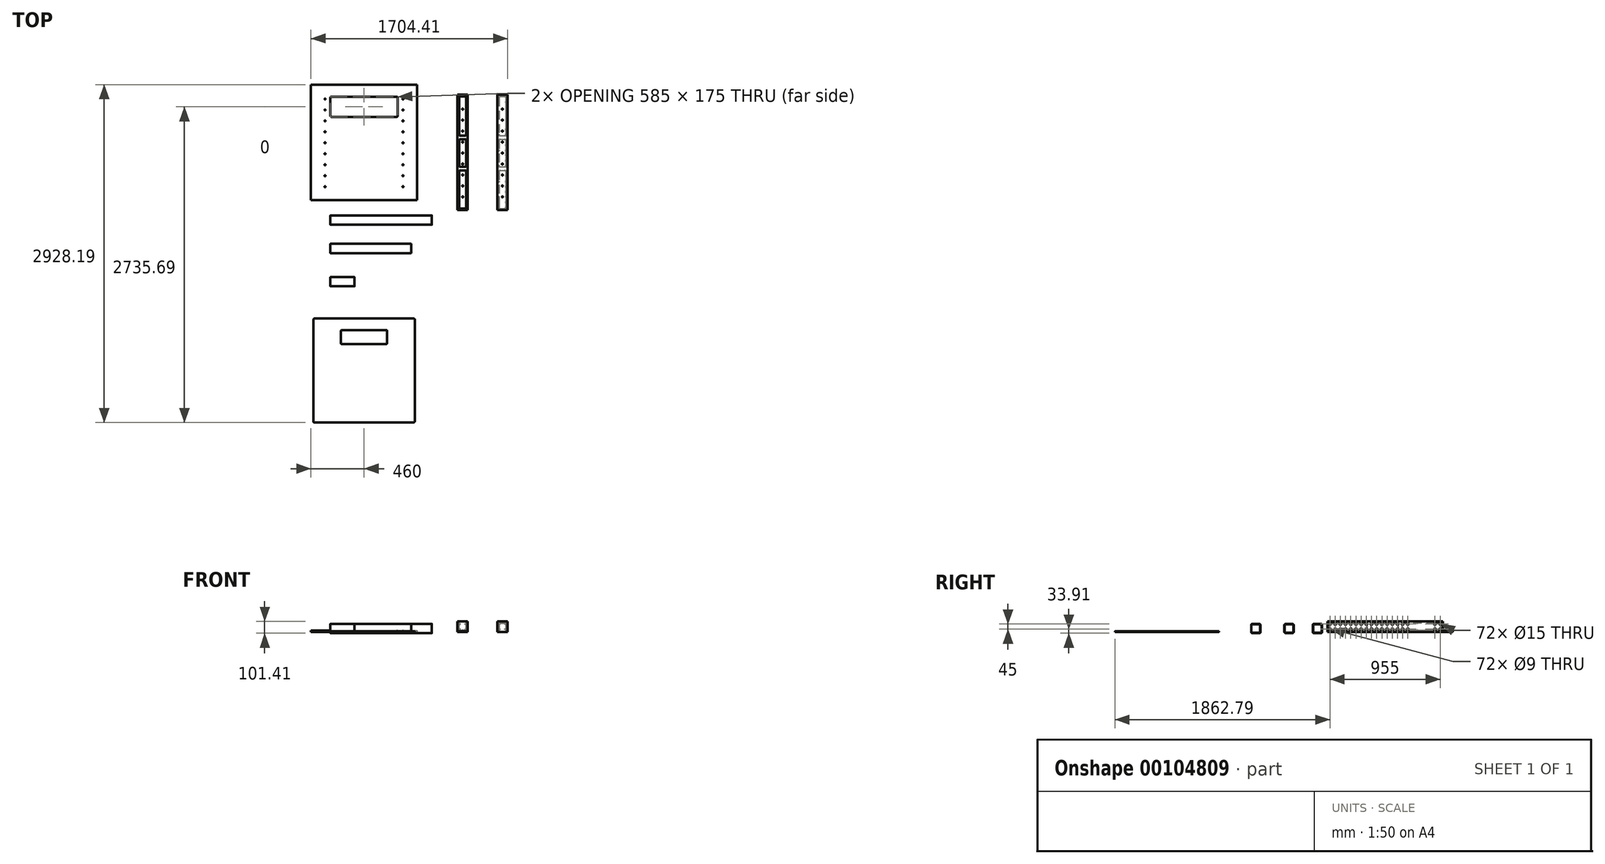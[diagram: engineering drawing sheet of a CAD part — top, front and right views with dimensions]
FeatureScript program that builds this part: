
annotation { "Feature Type Name" : "Feature", "Feature Type Description" : "" }
export const myFeature = defineFeature(function(context is Context, id is Id, definition is map)
    precondition{}
    {
        {
            var Q0;
            Q0=qCreatedBy(makeId("Top.planeOp"),FACE);
            var sketch = newSketch(context, id + "F0", { "sketchPlane" : qUnion([Q0])});
            skLineSegment(sketch, "E0.bottom", {"start": v(-167.5, 789.91) * mm, "end": v(752.5, 789.91) * mm});
            skLineSegment(sketch, "E0.top", {"start": v(-167.5, -210.09) * mm, "end": v(752.5, -210.09) * mm});
            skLineSegment(sketch, "E0.left", {"start": v(-167.5, 789.91) * mm, "end": v(-167.5, -210.09) * mm});
            skLineSegment(sketch, "E0.right", {"start": v(752.5, 789.91) * mm, "end": v(752.5, -210.09) * mm});
            skLineSegment(sketch, "E1.bottom", {"start": v(10, 684.91) * mm, "end": v(575, 684.91) * mm});
            skLineSegment(sketch, "E1.top", {"start": v(10, 509.91) * mm, "end": v(575, 509.91) * mm});
            skLineSegment(sketch, "E1.left", {"start": v(0, 674.91) * mm, "end": v(0, 519.91) * mm});
            skLineSegment(sketch, "E1.right", {"start": v(585, 674.91) * mm, "end": v(585, 519.91) * mm});
            skPoint(sketch, "E2.visualSharp", {"position": v(0, 684.91) * mm});
            skArc(sketch, "E2.filletArc", {"start": v(10, 684.91) * mm, "mid": v(2.93, 681.98) * mm, "end": v(0, 674.91) * mm});
            skPoint(sketch, "E3.visualSharp", {"position": v(0, 509.91) * mm});
            skArc(sketch, "E3.filletArc", {"start": v(0, 519.91) * mm, "mid": v(2.93, 512.84) * mm, "end": v(10, 509.91) * mm});
            skPoint(sketch, "E4.visualSharp", {"position": v(585, 684.91) * mm});
            skArc(sketch, "E4.filletArc", {"start": v(585, 674.91) * mm, "mid": v(582.07, 681.98) * mm, "end": v(575, 684.91) * mm});
            skPoint(sketch, "E5.visualSharp", {"position": v(585, 509.91) * mm});
            skArc(sketch, "E5.filletArc", {"start": v(575, 509.91) * mm, "mid": v(582.07, 512.84) * mm, "end": v(585, 519.91) * mm});
            skLineSegment(sketch, "E6.bottom", {"start": v(1101.91, 702) * mm, "end": v(1191.91, 702) * mm});
            skLineSegment(sketch, "E6.top", {"start": v(1101.91, -298) * mm, "end": v(1191.91, -298) * mm});
            skLineSegment(sketch, "E6.left", {"start": v(1101.91, 702) * mm, "end": v(1101.91, -298) * mm});
            skLineSegment(sketch, "E6.right", {"start": v(1191.91, 702) * mm, "end": v(1191.91, -298) * mm});
            skPoint(sketch, "E7", {"position": v(292.5, 684.91) * mm});
            skPoint(sketch, "E8", {"position": v(292.5, 789.91) * mm});
            skLineSegment(sketch, "E9.bottom", {"start": v(-137.5, -1238.28) * mm, "end": v(722.5, -1238.28) * mm});
            skLineSegment(sketch, "E9.top", {"start": v(-137.5, -2138.28) * mm, "end": v(722.5, -2138.28) * mm});
            skLineSegment(sketch, "E9.left", {"start": v(-147.5, -1248.28) * mm, "end": v(-147.5, -2128.28) * mm});
            skLineSegment(sketch, "E9.right", {"start": v(732.5, -1248.28) * mm, "end": v(732.5, -2128.28) * mm});
            skLineSegment(sketch, "E10.bottom", {"start": v(97.5, -1338.28) * mm, "end": v(487.5, -1338.28) * mm});
            skLineSegment(sketch, "E10.top", {"start": v(97.5, -1458.28) * mm, "end": v(487.5, -1458.28) * mm});
            skLineSegment(sketch, "E10.left", {"start": v(92.5, -1343.28) * mm, "end": v(92.5, -1453.28) * mm});
            skLineSegment(sketch, "E10.right", {"start": v(492.5, -1343.28) * mm, "end": v(492.5, -1453.28) * mm});
            skPoint(sketch, "E11.visualSharp", {"position": v(92.5, -1338.28) * mm});
            skArc(sketch, "E11.filletArc", {"start": v(97.5, -1338.28) * mm, "mid": v(93.97, -1339.74) * mm, "end": v(92.5, -1343.28) * mm});
            skPoint(sketch, "E12.visualSharp", {"position": v(92.5, -1458.28) * mm});
            skArc(sketch, "E12.filletArc", {"start": v(92.5, -1453.28) * mm, "mid": v(93.97, -1456.81) * mm, "end": v(97.5, -1458.28) * mm});
            skPoint(sketch, "E13.visualSharp", {"position": v(492.5, -1458.28) * mm});
            skArc(sketch, "E13.filletArc", {"start": v(487.5, -1458.28) * mm, "mid": v(491.04, -1456.81) * mm, "end": v(492.5, -1453.28) * mm});
            skPoint(sketch, "E14.visualSharp", {"position": v(492.5, -1338.28) * mm});
            skArc(sketch, "E14.filletArc", {"start": v(492.5, -1343.28) * mm, "mid": v(491.04, -1339.74) * mm, "end": v(487.5, -1338.28) * mm});
            skPoint(sketch, "E15.visualSharp", {"position": v(-147.5, -2138.28) * mm});
            skArc(sketch, "E15.filletArc", {"start": v(-147.5, -2128.28) * mm, "mid": v(-144.56, -2135.35) * mm, "end": v(-137.5, -2138.28) * mm});
            skPoint(sketch, "E16.visualSharp", {"position": v(732.5, -2138.28) * mm});
            skArc(sketch, "E16.filletArc", {"start": v(722.5, -2138.28) * mm, "mid": v(729.58, -2135.35) * mm, "end": v(732.5, -2128.28) * mm});
            skPoint(sketch, "E17.visualSharp", {"position": v(732.5, -1238.28) * mm});
            skArc(sketch, "E17.filletArc", {"start": v(732.5, -1248.28) * mm, "mid": v(729.58, -1241.2) * mm, "end": v(722.5, -1238.28) * mm});
            skPoint(sketch, "E18.visualSharp", {"position": v(-147.5, -1238.28) * mm});
            skArc(sketch, "E18.filletArc", {"start": v(-137.5, -1238.28) * mm, "mid": v(-144.56, -1241.2) * mm, "end": v(-147.5, -1248.28) * mm});
            skSolve(sketch);
        }
        {
            var Q0;
            Q0=makeQuery(id+"F0.imprint","IMPRINT",FACE,{"disambiguationData":[TD([[makeQuery(id+"F0.imprint","IMPRINT",EDGE,{"derivedFrom":sQuery(id+"F0.wireOp",EDGE,"E0.bottom")}),-1.0]])]});
            extrude(context, id + "F1", {"entities" : qUnion([Q0]), "depth" : 10 * mm});
        }
        {
            var Q0;
            Q0=makeQuery(id+"F0.imprint","IMPRINT",FACE,{"disambiguationData":[TD([[makeQuery(id+"F0.imprint","IMPRINT",EDGE,{"derivedFrom":sQuery(id+"F0.wireOp",EDGE,"E6.bottom")}),-1.0]])]});
            extrude(context, id + "F2", {"entities" : qUnion([Q0]), "depth" : 90 * mm});
        }
        {
            var Q0;
            Q0=makeQuery(id+"F2.opExtrude","SWEPT_FACE",FACE,{"disambiguationData":[OSD([sQuery(id+"F0.wireOp",EDGE,"E6.right")])]});
            var sketch = newSketch(context, id + "F3", { "sketchPlane" : qUnion([Q0])});
            skLineSegment(sketch, "E19", {"start": v(-298, 67.5) * mm, "end": v(702, 67.5) * mm});
            skLineSegment(sketch, "E20", {"start": v(-298, 22.5) * mm, "end": v(702, 22.5) * mm});
            skLineSegment(sketch, "E21", {"start": v(-275.5, 90) * mm, "end": v(-275.5, 0) * mm});
            skLineSegment(sketch, "E22", {"start": v(-230.5, 90) * mm, "end": v(-230.5, 0) * mm});
            skLineSegment(sketch, "E23", {"start": v(-185.5, 90) * mm, "end": v(-185.5, 0) * mm});
            skLineSegment(sketch, "E24", {"start": v(-140.5, 90) * mm, "end": v(-140.5, 0) * mm});
            skPoint(sketch, "E25", {"position": v(-275.5, 67.5) * mm});
            skPoint(sketch, "E26", {"position": v(-230.5, 67.5) * mm});
            skPoint(sketch, "E27", {"position": v(-140.5, 67.5) * mm});
            skPoint(sketch, "E28", {"position": v(-185.5, 67.5) * mm});
            skPoint(sketch, "E29", {"position": v(-185.5, 22.5) * mm});
            skPoint(sketch, "E30", {"position": v(-140.5, 22.5) * mm});
            skPoint(sketch, "E31", {"position": v(-230.5, 22.5) * mm});
            skPoint(sketch, "E32", {"position": v(-275.5, 22.5) * mm});
            skLineSegment(sketch, "E33", {"start": v(-95.5, 90) * mm, "end": v(-95.5, 0) * mm});
            skLineSegment(sketch, "E34", {"start": v(-50.5, 90) * mm, "end": v(-50.5, 0) * mm});
            skLineSegment(sketch, "E35", {"start": v(-5.5, 90) * mm, "end": v(-5.5, 0) * mm});
            skLineSegment(sketch, "E36", {"start": v(39.5, 90) * mm, "end": v(39.5, 0) * mm});
            skLineSegment(sketch, "E37", {"start": v(84.5, 90) * mm, "end": v(84.5, 0) * mm});
            skLineSegment(sketch, "E38", {"start": v(129.5, 90) * mm, "end": v(129.5, 0) * mm});
            skLineSegment(sketch, "E39", {"start": v(174.5, 90) * mm, "end": v(174.5, 0) * mm});
            skLineSegment(sketch, "E40", {"start": v(219.5, 90) * mm, "end": v(219.5, 0) * mm});
            skLineSegment(sketch, "E41", {"start": v(264.5, 90) * mm, "end": v(264.5, 0) * mm});
            skLineSegment(sketch, "E42", {"start": v(309.5, 90) * mm, "end": v(309.5, 0) * mm});
            skPoint(sketch, "E43", {"position": v(-95.5, 67.5) * mm});
            skPoint(sketch, "E44", {"position": v(-95.5, 22.5) * mm});
            skPoint(sketch, "E45", {"position": v(-50.5, 67.5) * mm});
            skPoint(sketch, "E46", {"position": v(-50.5, 22.5) * mm});
            skPoint(sketch, "E47", {"position": v(-5.5, 67.5) * mm});
            skPoint(sketch, "E48", {"position": v(-5.5, 22.5) * mm});
            skPoint(sketch, "E49", {"position": v(39.5, 67.5) * mm});
            skPoint(sketch, "E50", {"position": v(39.5, 22.5) * mm});
            skPoint(sketch, "E51", {"position": v(84.5, 67.5) * mm});
            skPoint(sketch, "E52", {"position": v(84.5, 22.5) * mm});
            skPoint(sketch, "E53", {"position": v(129.5, 67.5) * mm});
            skPoint(sketch, "E54", {"position": v(129.5, 22.5) * mm});
            skPoint(sketch, "E55", {"position": v(174.5, 67.5) * mm});
            skPoint(sketch, "E56", {"position": v(174.5, 22.5) * mm});
            skPoint(sketch, "E57", {"position": v(219.5, 67.5) * mm});
            skPoint(sketch, "E58", {"position": v(219.5, 22.5) * mm});
            skPoint(sketch, "E59", {"position": v(264.5, 67.5) * mm});
            skPoint(sketch, "E60", {"position": v(264.5, 22.5) * mm});
            skPoint(sketch, "E61", {"position": v(309.5, 22.5) * mm});
            skPoint(sketch, "E62", {"position": v(309.5, 67.5) * mm});
            skLineSegment(sketch, "E63", {"start": v(679.5, 90) * mm, "end": v(679.5, 0) * mm});
            skLineSegment(sketch, "E64", {"start": v(634.5, 90) * mm, "end": v(634.5, 0) * mm});
            skPoint(sketch, "E65", {"position": v(634.5, 67.5) * mm});
            skPoint(sketch, "E66", {"position": v(634.5, 22.5) * mm});
            skPoint(sketch, "E67", {"position": v(679.5, 67.5) * mm});
            skPoint(sketch, "E68", {"position": v(679.5, 22.5) * mm});
            skLineSegment(sketch, "E69", {"start": v(354.5, 0) * mm, "end": v(354.5, 90) * mm});
            skLineSegment(sketch, "E70", {"start": v(399.5, 0) * mm, "end": v(399.5, 90) * mm});
            skPoint(sketch, "E71", {"position": v(399.5, 22.5) * mm});
            skPoint(sketch, "E72", {"position": v(354.5, 22.5) * mm});
            skPoint(sketch, "E73", {"position": v(354.5, 67.5) * mm});
            skPoint(sketch, "E74", {"position": v(399.5, 67.5) * mm});
            skSolve(sketch);
        }
        {
            var Q0;
            Q0=sQuery(id+"F3.wireOp",VERTEX,"E25");
            var Q1;
            Q1=sQuery(id+"F3.wireOp",VERTEX,"E32");
            var Q2;
            Q2=sQuery(id+"F3.wireOp",VERTEX,"E26");
            var Q3;
            Q3=sQuery(id+"F3.wireOp",VERTEX,"E31");
            var Q4;
            Q4=sQuery(id+"F3.wireOp",VERTEX,"E28");
            var Q5;
            Q5=sQuery(id+"F3.wireOp",VERTEX,"E29");
            var Q6;
            Q6=sQuery(id+"F3.wireOp",VERTEX,"E30");
            var Q7;
            Q7=sQuery(id+"F3.wireOp",VERTEX,"E27");
            var Q8;
            Q8=sQuery(id+"F3.wireOp",VERTEX,"E43");
            var Q9;
            Q9=sQuery(id+"F3.wireOp",VERTEX,"E44");
            var Q10;
            Q10=sQuery(id+"F3.wireOp",VERTEX,"E46");
            var Q11;
            Q11=sQuery(id+"F3.wireOp",VERTEX,"E45");
            var Q12;
            Q12=sQuery(id+"F3.wireOp",VERTEX,"E47");
            var Q13;
            Q13=sQuery(id+"F3.wireOp",VERTEX,"E48");
            var Q14;
            Q14=sQuery(id+"F3.wireOp",VERTEX,"E50");
            var Q15;
            Q15=sQuery(id+"F3.wireOp",VERTEX,"E49");
            var Q16;
            Q16=sQuery(id+"F3.wireOp",VERTEX,"E51");
            var Q17;
            Q17=sQuery(id+"F3.wireOp",VERTEX,"E52");
            var Q18;
            Q18=sQuery(id+"F3.wireOp",VERTEX,"E54");
            var Q19;
            Q19=sQuery(id+"F3.wireOp",VERTEX,"E53");
            var Q20;
            Q20=sQuery(id+"F3.wireOp",VERTEX,"E55");
            var Q21;
            Q21=sQuery(id+"F3.wireOp",VERTEX,"E56");
            var Q22;
            Q22=sQuery(id+"F3.wireOp",VERTEX,"E58");
            var Q23;
            Q23=sQuery(id+"F3.wireOp",VERTEX,"E57");
            var Q24;
            Q24=sQuery(id+"F3.wireOp",VERTEX,"E59");
            var Q25;
            Q25=sQuery(id+"F3.wireOp",VERTEX,"E60");
            var Q26;
            Q26=sQuery(id+"F3.wireOp",VERTEX,"E61");
            var Q27;
            Q27=sQuery(id+"F3.wireOp",VERTEX,"E62");
            var Q28;
            Q28=sQuery(id+"F3.wireOp",VERTEX,"E65");
            var Q29;
            Q29=sQuery(id+"F3.wireOp",VERTEX,"E66");
            var Q30;
            Q30=sQuery(id+"F3.wireOp",VERTEX,"E68");
            var Q31;
            Q31=sQuery(id+"F3.wireOp",VERTEX,"E67");
            var Q32;
            Q32=sQuery(id+"F3.wireOp",VERTEX,"E72");
            var Q33;
            Q33=sQuery(id+"F3.wireOp",VERTEX,"E73");
            var Q34;
            Q34=sQuery(id+"F3.wireOp",VERTEX,"E71");
            var Q35;
            Q35=sQuery(id+"F3.wireOp",VERTEX,"E74");
            var Q36;
            Q36=makeQuery(id+"F2.opExtrude","SWEPT_BODY",BODY,{"disambiguationData":[OSD([sQuery(id+"F0.wireOp",EDGE,"E6.bottom"),sQuery(id+"F0.wireOp",EDGE,"E6.top"),sQuery(id+"F0.wireOp",EDGE,"E6.left"),sQuery(id+"F0.wireOp",EDGE,"E6.right")])]});
            hole(context, id + "F4", {"style" : HoleStyle.C_BORE, "endStyle" : HoleEndStyle.THROUGH, "holeDiameter" : 9 * mm, "cBoreDiameter" : 15 * mm, "cBoreDepth" : 75 * mm, "locations" : qUnion([Q0, Q1, Q2, Q3, Q4, Q5, Q6, Q7, Q8, Q9, Q10, Q11, Q12, Q13, Q14, Q15, Q16, Q17, Q18, Q19, Q20, Q21, Q22, Q23, Q24, Q25, Q26, Q27, Q28, Q29, Q30, Q31, Q32, Q33, Q34, Q35]), "scope" : qUnion([Q36]), "isTappedThrough" : true});
        }
        {
            var Q0;
            Q0=makeQuery(id+"F2.opExtrude","CAP_FACE",FACE,{"disambiguationData":[OSD([sQuery(id+"F0.wireOp",EDGE,"E6.bottom"),sQuery(id+"F0.wireOp",EDGE,"E6.top"),sQuery(id+"F0.wireOp",EDGE,"E6.left"),sQuery(id+"F0.wireOp",EDGE,"E6.right")])],"isStart":false});
            var sketch = newSketch(context, id + "F5", { "sketchPlane" : qUnion([Q0])});
            skLineSegment(sketch, "E75", {"start": v(1146.91, -298) * mm, "end": v(1146.91, 702) * mm});
            skLineSegment(sketch, "E76", {"start": v(1101.91, -203) * mm, "end": v(1191.91, -203) * mm});
            skLineSegment(sketch, "E77", {"start": v(1101.91, -88) * mm, "end": v(1191.91, -88) * mm});
            skLineSegment(sketch, "E78", {"start": v(1101.91, 7) * mm, "end": v(1191.91, 7) * mm});
            skLineSegment(sketch, "E79", {"start": v(1101.91, 102) * mm, "end": v(1191.91, 102) * mm});
            skLineSegment(sketch, "E80", {"start": v(1101.91, 292) * mm, "end": v(1191.91, 292) * mm});
            skLineSegment(sketch, "E81", {"start": v(1101.91, 197) * mm, "end": v(1191.91, 197) * mm});
            skLineSegment(sketch, "E82", {"start": v(1101.91, 387) * mm, "end": v(1191.91, 387) * mm});
            skLineSegment(sketch, "E83", {"start": v(1101.91, 482) * mm, "end": v(1191.91, 482) * mm});
            skLineSegment(sketch, "E84", {"start": v(1101.91, -183) * mm, "end": v(1191.91, -183) * mm});
            skLineSegment(sketch, "E85", {"start": v(1101.91, 577) * mm, "end": v(1191.91, 577) * mm});
            skPoint(sketch, "E86", {"position": v(1146.91, -183) * mm});
            skPoint(sketch, "E87", {"position": v(1146.91, -88) * mm});
            skPoint(sketch, "E88", {"position": v(1146.91, 7) * mm});
            skPoint(sketch, "E89", {"position": v(1146.91, 102) * mm});
            skPoint(sketch, "E90", {"position": v(1146.91, 197) * mm});
            skPoint(sketch, "E91", {"position": v(1146.91, 292) * mm});
            skPoint(sketch, "E92", {"position": v(1146.91, 387) * mm});
            skPoint(sketch, "E93", {"position": v(1146.91, 482) * mm});
            skPoint(sketch, "E94", {"position": v(1146.91, 577) * mm});
            skLineSegment(sketch, "E95.bottom", {"start": v(1126.91, -283) * mm, "end": v(1166.91, -283) * mm});
            skLineSegment(sketch, "E95.top", {"start": v(1126.91, 47) * mm, "end": v(1166.91, 47) * mm});
            skLineSegment(sketch, "E95.left", {"start": v(1116.91, -273) * mm, "end": v(1116.91, 37) * mm});
            skLineSegment(sketch, "E95.right", {"start": v(1176.91, -273) * mm, "end": v(1176.91, 37) * mm});
            skLineSegment(sketch, "E96.bottom", {"start": v(1126.91, 77) * mm, "end": v(1166.91, 77) * mm});
            skLineSegment(sketch, "E96.top", {"start": v(1126.91, 317) * mm, "end": v(1166.91, 317) * mm});
            skLineSegment(sketch, "E96.left", {"start": v(1116.91, 87) * mm, "end": v(1116.91, 307) * mm});
            skLineSegment(sketch, "E96.right", {"start": v(1176.91, 87) * mm, "end": v(1176.91, 307) * mm});
            skLineSegment(sketch, "E97.bottom", {"start": v(1126.91, 347) * mm, "end": v(1166.91, 347) * mm});
            skLineSegment(sketch, "E97.top", {"start": v(1126.91, 687) * mm, "end": v(1166.91, 687) * mm});
            skLineSegment(sketch, "E97.left", {"start": v(1116.91, 357) * mm, "end": v(1116.91, 677) * mm});
            skLineSegment(sketch, "E97.right", {"start": v(1176.91, 357) * mm, "end": v(1176.91, 677) * mm});
            skPoint(sketch, "E98.visualSharp", {"position": v(1116.91, -283) * mm});
            skArc(sketch, "E98.filletArc", {"start": v(1116.91, -273) * mm, "mid": v(1119.84, -280.06) * mm, "end": v(1126.91, -283) * mm});
            skPoint(sketch, "E99.visualSharp", {"position": v(1176.91, -283) * mm});
            skArc(sketch, "E99.filletArc", {"start": v(1166.91, -283) * mm, "mid": v(1173.98, -280.06) * mm, "end": v(1176.91, -273) * mm});
            skPoint(sketch, "E100.visualSharp", {"position": v(1176.91, 47) * mm});
            skArc(sketch, "E100.filletArc", {"start": v(1176.91, 37) * mm, "mid": v(1173.98, 44.08) * mm, "end": v(1166.91, 47) * mm});
            skPoint(sketch, "E101.visualSharp", {"position": v(1116.91, 47) * mm});
            skArc(sketch, "E101.filletArc", {"start": v(1126.91, 47) * mm, "mid": v(1119.84, 44.08) * mm, "end": v(1116.91, 37) * mm});
            skPoint(sketch, "E102.visualSharp", {"position": v(1116.91, 77) * mm});
            skArc(sketch, "E102.filletArc", {"start": v(1116.91, 87) * mm, "mid": v(1119.84, 79.94) * mm, "end": v(1126.91, 77) * mm});
            skPoint(sketch, "E103.visualSharp", {"position": v(1176.91, 77) * mm});
            skArc(sketch, "E103.filletArc", {"start": v(1166.91, 77) * mm, "mid": v(1173.98, 79.94) * mm, "end": v(1176.91, 87) * mm});
            skPoint(sketch, "E104.visualSharp", {"position": v(1116.91, 317) * mm});
            skArc(sketch, "E104.filletArc", {"start": v(1126.91, 317) * mm, "mid": v(1119.84, 314.08) * mm, "end": v(1116.91, 307) * mm});
            skPoint(sketch, "E105.visualSharp", {"position": v(1176.91, 317) * mm});
            skArc(sketch, "E105.filletArc", {"start": v(1176.91, 307) * mm, "mid": v(1173.98, 314.08) * mm, "end": v(1166.91, 317) * mm});
            skPoint(sketch, "E106.visualSharp", {"position": v(1176.91, 347) * mm});
            skArc(sketch, "E106.filletArc", {"start": v(1166.91, 347) * mm, "mid": v(1173.98, 349.94) * mm, "end": v(1176.91, 357) * mm});
            skPoint(sketch, "E107.visualSharp", {"position": v(1116.91, 347) * mm});
            skArc(sketch, "E107.filletArc", {"start": v(1116.91, 357) * mm, "mid": v(1119.84, 349.94) * mm, "end": v(1126.91, 347) * mm});
            skPoint(sketch, "E108.visualSharp", {"position": v(1116.91, 687) * mm});
            skArc(sketch, "E108.filletArc", {"start": v(1126.91, 687) * mm, "mid": v(1119.84, 684.08) * mm, "end": v(1116.91, 677) * mm});
            skPoint(sketch, "E109.visualSharp", {"position": v(1176.91, 687) * mm});
            skArc(sketch, "E109.filletArc", {"start": v(1176.91, 677) * mm, "mid": v(1173.98, 684.08) * mm, "end": v(1166.91, 687) * mm});
            skSolve(sketch);
        }
        {
            var Q0;
            Q0=makeQuery(id+"F2.opExtrude","SWEPT_BODY",BODY,{"disambiguationData":[OSD([sQuery(id+"F0.wireOp",EDGE,"E6.bottom"),sQuery(id+"F0.wireOp",EDGE,"E6.top"),sQuery(id+"F0.wireOp",EDGE,"E6.left"),sQuery(id+"F0.wireOp",EDGE,"E6.right")])]});
            transform(context, id + "F6", {"entities" : qUnion([Q0]), "transformType" : TransformType.TRANSLATION_3D, "dx" : 345 * mm, "dy" : 0 * mm, "dz" : 0 * mm, "makeCopy" : true});
        }
        {
            var Q0;
            Q0=sQuery(id+"F5.wireOp",VERTEX,"E86");
            var Q1;
            Q1=sQuery(id+"F5.wireOp",VERTEX,"E87");
            var Q2;
            Q2=sQuery(id+"F5.wireOp",VERTEX,"E88");
            var Q3;
            Q3=sQuery(id+"F5.wireOp",VERTEX,"E89");
            var Q4;
            Q4=sQuery(id+"F5.wireOp",VERTEX,"E90");
            var Q5;
            Q5=sQuery(id+"F5.wireOp",VERTEX,"E91");
            var Q6;
            Q6=sQuery(id+"F5.wireOp",VERTEX,"E92");
            var Q7;
            Q7=sQuery(id+"F5.wireOp",VERTEX,"E93");
            var Q8;
            Q8=sQuery(id+"F5.wireOp",VERTEX,"E94");
            var Q9;
            Q9=makeQuery(id+"F2.opExtrude","SWEPT_BODY",BODY,{"disambiguationData":[OSD([sQuery(id+"F0.wireOp",EDGE,"E6.bottom"),sQuery(id+"F0.wireOp",EDGE,"E6.top"),sQuery(id+"F0.wireOp",EDGE,"E6.left"),sQuery(id+"F0.wireOp",EDGE,"E6.right")])]});
            hole(context, id + "F7", {"style" : HoleStyle.C_BORE, "endStyle" : HoleEndStyle.THROUGH, "holeDiameter" : 9.5 * mm, "cBoreDiameter" : 15 * mm, "cBoreDepth" : 75 * mm, "locations" : qUnion([Q0, Q1, Q2, Q3, Q4, Q5, Q6, Q7, Q8]), "scope" : qUnion([Q9]), "isTappedThrough" : true});
        }
        {
            var Q0;
            Q0=makeQuery(id+"F6.opPattern","COPY",FACE,{"derivedFrom":makeQuery(id+"F2.opExtrude","CAP_FACE",FACE,{"disambiguationData":[OSD([sQuery(id+"F0.wireOp",EDGE,"E6.bottom"),sQuery(id+"F0.wireOp",EDGE,"E6.top"),sQuery(id+"F0.wireOp",EDGE,"E6.left"),sQuery(id+"F0.wireOp",EDGE,"E6.right")])],"isStart":true}),"instanceName":"1"});
            var sketch = newSketch(context, id + "F8", { "sketchPlane" : qUnion([Q0])});
            skLineSegment(sketch, "E110", {"start": v(1446.91, -577) * mm, "end": v(1536.91, -577) * mm});
            skLineSegment(sketch, "E111", {"start": v(1446.91, -482) * mm, "end": v(1536.91, -482) * mm});
            skLineSegment(sketch, "E112", {"start": v(1446.91, -387) * mm, "end": v(1536.91, -387) * mm});
            skLineSegment(sketch, "E113", {"start": v(1446.91, -292) * mm, "end": v(1536.91, -292) * mm});
            skLineSegment(sketch, "E114", {"start": v(1446.91, -197) * mm, "end": v(1536.91, -197) * mm});
            skLineSegment(sketch, "E115", {"start": v(1446.91, -102) * mm, "end": v(1536.91, -102) * mm});
            skLineSegment(sketch, "E116", {"start": v(1446.91, -7) * mm, "end": v(1536.91, -7) * mm});
            skLineSegment(sketch, "E117", {"start": v(1446.91, 88) * mm, "end": v(1536.91, 88) * mm});
            skLineSegment(sketch, "E118", {"start": v(1446.91, 183) * mm, "end": v(1536.91, 183) * mm});
            skLineSegment(sketch, "E119", {"start": v(1446.91, 203) * mm, "end": v(1536.91, 203) * mm});
            skLineSegment(sketch, "E120", {"start": v(1491.91, -702) * mm, "end": v(1491.91, 298) * mm});
            skPoint(sketch, "E121", {"position": v(1491.91, -577) * mm});
            skPoint(sketch, "E122", {"position": v(1491.91, -482) * mm});
            skPoint(sketch, "E123", {"position": v(1491.91, -387) * mm});
            skPoint(sketch, "E124", {"position": v(1491.91, -292) * mm});
            skPoint(sketch, "E125", {"position": v(1491.91, -197) * mm});
            skPoint(sketch, "E126", {"position": v(1491.91, -102) * mm});
            skPoint(sketch, "E127", {"position": v(1491.91, -7) * mm});
            skPoint(sketch, "E128", {"position": v(1491.91, 88) * mm});
            skPoint(sketch, "E129", {"position": v(1491.91, 183) * mm});
            skLineSegment(sketch, "E130.bottom", {"start": v(1471.91, -687) * mm, "end": v(1511.91, -687) * mm});
            skLineSegment(sketch, "E130.top", {"start": v(1471.91, -347) * mm, "end": v(1511.91, -347) * mm});
            skLineSegment(sketch, "E130.left", {"start": v(1461.91, -677) * mm, "end": v(1461.91, -357) * mm});
            skLineSegment(sketch, "E130.right", {"start": v(1521.91, -677) * mm, "end": v(1521.91, -357) * mm});
            skLineSegment(sketch, "E131.bottom", {"start": v(1471.91, -317) * mm, "end": v(1511.91, -317) * mm});
            skLineSegment(sketch, "E131.top", {"start": v(1471.91, -77) * mm, "end": v(1511.91, -77) * mm});
            skLineSegment(sketch, "E131.left", {"start": v(1461.91, -307) * mm, "end": v(1461.91, -87) * mm});
            skLineSegment(sketch, "E131.right", {"start": v(1521.91, -307) * mm, "end": v(1521.91, -87) * mm});
            skLineSegment(sketch, "E132.bottom", {"start": v(1471.91, -47) * mm, "end": v(1511.91, -47) * mm});
            skLineSegment(sketch, "E132.top", {"start": v(1471.91, 283) * mm, "end": v(1511.91, 283) * mm});
            skLineSegment(sketch, "E132.left", {"start": v(1461.91, -37) * mm, "end": v(1461.91, 273) * mm});
            skLineSegment(sketch, "E132.right", {"start": v(1521.91, -37) * mm, "end": v(1521.91, 273) * mm});
            skPoint(sketch, "E133.visualSharp", {"position": v(1461.91, 283) * mm});
            skArc(sketch, "E133.filletArc", {"start": v(1471.91, 283) * mm, "mid": v(1464.84, 280.06) * mm, "end": v(1461.91, 273) * mm});
            skPoint(sketch, "E134.visualSharp", {"position": v(1521.91, 283) * mm});
            skArc(sketch, "E134.filletArc", {"start": v(1521.91, 273) * mm, "mid": v(1518.98, 280.06) * mm, "end": v(1511.91, 283) * mm});
            skPoint(sketch, "E135.visualSharp", {"position": v(1461.91, -47) * mm});
            skArc(sketch, "E135.filletArc", {"start": v(1461.91, -37) * mm, "mid": v(1464.84, -44.08) * mm, "end": v(1471.91, -47) * mm});
            skPoint(sketch, "E136.visualSharp", {"position": v(1521.91, -47) * mm});
            skArc(sketch, "E136.filletArc", {"start": v(1511.91, -47) * mm, "mid": v(1518.98, -44.08) * mm, "end": v(1521.91, -37) * mm});
            skPoint(sketch, "E137.visualSharp", {"position": v(1461.91, -77) * mm});
            skArc(sketch, "E137.filletArc", {"start": v(1471.91, -77) * mm, "mid": v(1464.84, -79.94) * mm, "end": v(1461.91, -87) * mm});
            skPoint(sketch, "E138.visualSharp", {"position": v(1521.91, -77) * mm});
            skArc(sketch, "E138.filletArc", {"start": v(1521.91, -87) * mm, "mid": v(1518.98, -79.94) * mm, "end": v(1511.91, -77) * mm});
            skPoint(sketch, "E139.visualSharp", {"position": v(1521.91, -317) * mm});
            skArc(sketch, "E139.filletArc", {"start": v(1511.91, -317) * mm, "mid": v(1518.98, -314.08) * mm, "end": v(1521.91, -307) * mm});
            skPoint(sketch, "E140.visualSharp", {"position": v(1461.91, -317) * mm});
            skArc(sketch, "E140.filletArc", {"start": v(1461.91, -307) * mm, "mid": v(1464.84, -314.08) * mm, "end": v(1471.91, -317) * mm});
            skPoint(sketch, "E141.visualSharp", {"position": v(1461.91, -347) * mm});
            skArc(sketch, "E141.filletArc", {"start": v(1471.91, -347) * mm, "mid": v(1464.84, -349.94) * mm, "end": v(1461.91, -357) * mm});
            skPoint(sketch, "E142.visualSharp", {"position": v(1521.91, -347) * mm});
            skArc(sketch, "E142.filletArc", {"start": v(1521.91, -357) * mm, "mid": v(1518.98, -349.94) * mm, "end": v(1511.91, -347) * mm});
            skPoint(sketch, "E143.visualSharp", {"position": v(1521.91, -687) * mm});
            skArc(sketch, "E143.filletArc", {"start": v(1511.91, -687) * mm, "mid": v(1518.98, -684.08) * mm, "end": v(1521.91, -677) * mm});
            skPoint(sketch, "E144.visualSharp", {"position": v(1461.91, -687) * mm});
            skArc(sketch, "E144.filletArc", {"start": v(1461.91, -677) * mm, "mid": v(1464.84, -684.08) * mm, "end": v(1471.91, -687) * mm});
            skSolve(sketch);
        }
        {
            var Q0;
            Q0=sQuery(id+"F8.wireOp",VERTEX,"E121");
            var Q1;
            Q1=sQuery(id+"F8.wireOp",VERTEX,"E122");
            var Q2;
            Q2=sQuery(id+"F8.wireOp",VERTEX,"E123");
            var Q3;
            Q3=sQuery(id+"F8.wireOp",VERTEX,"E124");
            var Q4;
            Q4=sQuery(id+"F8.wireOp",VERTEX,"E125");
            var Q5;
            Q5=sQuery(id+"F8.wireOp",VERTEX,"E126");
            var Q6;
            Q6=sQuery(id+"F8.wireOp",VERTEX,"E127");
            var Q7;
            Q7=sQuery(id+"F8.wireOp",VERTEX,"E128");
            var Q8;
            Q8=sQuery(id+"F8.wireOp",VERTEX,"E129");
            var Q9;
            Q9=makeQuery(id+"F6.opPattern","COPY",BODY,{"derivedFrom":makeQuery(id+"F2.opExtrude","SWEPT_BODY",BODY,{"disambiguationData":[OSD([sQuery(id+"F0.wireOp",EDGE,"E6.bottom"),sQuery(id+"F0.wireOp",EDGE,"E6.top"),sQuery(id+"F0.wireOp",EDGE,"E6.left"),sQuery(id+"F0.wireOp",EDGE,"E6.right")])]}),"instanceName":"1"});
            hole(context, id + "F9", {"style" : HoleStyle.C_BORE, "endStyle" : HoleEndStyle.THROUGH, "holeDiameter" : 9.5 * mm, "cBoreDiameter" : 15 * mm, "cBoreDepth" : 75 * mm, "locations" : qUnion([Q0, Q1, Q2, Q3, Q4, Q5, Q6, Q7, Q8]), "scope" : qUnion([Q9]), "isTappedThrough" : true});
        }
        {
            var Q0;
            {var subQ0=sQuery(id+"F8.wireOp",EDGE,"E132.left");var subQ1=sQuery(id+"F8.wireOp",EDGE,"E117");var subQ2=makeQuery(id+"F8.imprint","INTERSECT",VERTEX,{"derivedFrom":[subQ1,subQ0]});Q0=makeQuery(id+"F8.imprint","IMPRINT",FACE,{"disambiguationData":[TD([[makeQuery(id+"F8.imprint","IMPRINT",EDGE,{"disambiguationData":[TD([[subQ2,-1.0]])],"derivedFrom":subQ1}),1.0]])]});}
            var Q1;
            {var subQ0=sQuery(id+"F8.wireOp",EDGE,"E132.left");var subQ1=sQuery(id+"F8.wireOp",EDGE,"E116");var subQ2=makeQuery(id+"F8.imprint","INTERSECT",VERTEX,{"derivedFrom":[subQ1,subQ0]});Q1=makeQuery(id+"F8.imprint","IMPRINT",FACE,{"disambiguationData":[TD([[makeQuery(id+"F8.imprint","IMPRINT",EDGE,{"disambiguationData":[TD([[subQ2,-1.0]])],"derivedFrom":subQ1}),1.0]])]});}
            var Q2;
            {var subQ0=sQuery(id+"F8.wireOp",EDGE,"E120");var subQ1=sQuery(id+"F8.wireOp",EDGE,"E116");var subQ2=makeQuery(id+"F8.imprint","INTERSECT",VERTEX,{"derivedFrom":[subQ1,subQ0]});Q2=makeQuery(id+"F8.imprint","IMPRINT",FACE,{"disambiguationData":[TD([[makeQuery(id+"F8.imprint","IMPRINT",EDGE,{"disambiguationData":[TD([[subQ2,-1.0]])],"derivedFrom":subQ1}),1.0]])]});}
            var Q3;
            {var subQ0=sQuery(id+"F8.wireOp",EDGE,"E120");var subQ1=sQuery(id+"F8.wireOp",EDGE,"E117");var subQ2=makeQuery(id+"F8.imprint","INTERSECT",VERTEX,{"derivedFrom":[subQ1,subQ0]});Q3=makeQuery(id+"F8.imprint","IMPRINT",FACE,{"disambiguationData":[TD([[makeQuery(id+"F8.imprint","IMPRINT",EDGE,{"disambiguationData":[TD([[subQ2,-1.0]])],"derivedFrom":subQ1}),1.0]])]});}
            var Q4;
            {var subQ0=sQuery(id+"F8.wireOp",EDGE,"E120");var subQ1=sQuery(id+"F8.wireOp",EDGE,"E118");var subQ2=makeQuery(id+"F8.imprint","INTERSECT",VERTEX,{"derivedFrom":[subQ1,subQ0]});Q4=makeQuery(id+"F8.imprint","IMPRINT",FACE,{"disambiguationData":[TD([[makeQuery(id+"F8.imprint","IMPRINT",EDGE,{"disambiguationData":[TD([[subQ2,-1.0]])],"derivedFrom":subQ1}),1.0]])]});}
            var Q5;
            {var subQ0=sQuery(id+"F8.wireOp",EDGE,"E132.left");var subQ1=sQuery(id+"F8.wireOp",EDGE,"E118");var subQ2=makeQuery(id+"F8.imprint","INTERSECT",VERTEX,{"derivedFrom":[subQ1,subQ0]});Q5=makeQuery(id+"F8.imprint","IMPRINT",FACE,{"disambiguationData":[TD([[makeQuery(id+"F8.imprint","IMPRINT",EDGE,{"disambiguationData":[TD([[subQ2,-1.0]])],"derivedFrom":subQ1}),1.0]])]});}
            var Q6;
            {var subQ0=sQuery(id+"F8.wireOp",EDGE,"E133.filletArc");Q6=makeQuery(id+"F8.imprint","IMPRINT",FACE,{"disambiguationData":[TD([[makeQuery(id+"F8.imprint","IMPRINT",EDGE,{"derivedFrom":subQ0}),1.0]])]});}
            var Q7;
            {var subQ0=sQuery(id+"F8.wireOp",EDGE,"E134.filletArc");Q7=makeQuery(id+"F8.imprint","IMPRINT",FACE,{"disambiguationData":[TD([[makeQuery(id+"F8.imprint","IMPRINT",EDGE,{"derivedFrom":subQ0}),1.0]])]});}
            var Q8;
            {var subQ5=sQuery(id+"F8.wireOp",EDGE,"E136.filletArc");Q8=makeQuery(id+"F8.imprint","IMPRINT",FACE,{"disambiguationData":[TD([[makeQuery(id+"F8.imprint","IMPRINT",EDGE,{"derivedFrom":subQ5}),1.0]])]});}
            var Q9;
            {var subQ0=sQuery(id+"F8.wireOp",EDGE,"E135.filletArc");Q9=makeQuery(id+"F8.imprint","IMPRINT",FACE,{"disambiguationData":[TD([[makeQuery(id+"F8.imprint","IMPRINT",EDGE,{"derivedFrom":subQ0}),1.0]])]});}
            var Q10;
            {var subQ0=sQuery(id+"F8.wireOp",EDGE,"E131.left");var subQ1=sQuery(id+"F8.wireOp",EDGE,"E114");var subQ2=makeQuery(id+"F8.imprint","INTERSECT",VERTEX,{"derivedFrom":[subQ1,subQ0]});Q10=makeQuery(id+"F8.imprint","IMPRINT",FACE,{"disambiguationData":[TD([[makeQuery(id+"F8.imprint","IMPRINT",EDGE,{"disambiguationData":[TD([[subQ2,-1.0]])],"derivedFrom":subQ1}),1.0]])]});}
            var Q11;
            {var subQ0=sQuery(id+"F8.wireOp",EDGE,"E120");var subQ1=sQuery(id+"F8.wireOp",EDGE,"E114");var subQ2=makeQuery(id+"F8.imprint","INTERSECT",VERTEX,{"derivedFrom":[subQ1,subQ0]});Q11=makeQuery(id+"F8.imprint","IMPRINT",FACE,{"disambiguationData":[TD([[makeQuery(id+"F8.imprint","IMPRINT",EDGE,{"disambiguationData":[TD([[subQ2,-1.0]])],"derivedFrom":subQ1}),1.0]])]});}
            var Q12;
            {var subQ0=sQuery(id+"F8.wireOp",EDGE,"E137.filletArc");Q12=makeQuery(id+"F8.imprint","IMPRINT",FACE,{"disambiguationData":[TD([[makeQuery(id+"F8.imprint","IMPRINT",EDGE,{"derivedFrom":subQ0}),1.0]])]});}
            var Q13;
            {var subQ0=sQuery(id+"F8.wireOp",EDGE,"E138.filletArc");Q13=makeQuery(id+"F8.imprint","IMPRINT",FACE,{"disambiguationData":[TD([[makeQuery(id+"F8.imprint","IMPRINT",EDGE,{"derivedFrom":subQ0}),1.0]])]});}
            var Q14;
            {var subQ0=sQuery(id+"F8.wireOp",EDGE,"E120");var subQ1=sQuery(id+"F8.wireOp",EDGE,"E113");var subQ2=makeQuery(id+"F8.imprint","INTERSECT",VERTEX,{"derivedFrom":[subQ1,subQ0]});Q14=makeQuery(id+"F8.imprint","IMPRINT",FACE,{"disambiguationData":[TD([[makeQuery(id+"F8.imprint","IMPRINT",EDGE,{"disambiguationData":[TD([[subQ2,-1.0]])],"derivedFrom":subQ1}),1.0]])]});}
            var Q15;
            {var subQ0=sQuery(id+"F8.wireOp",EDGE,"E131.left");var subQ1=sQuery(id+"F8.wireOp",EDGE,"E113");var subQ2=makeQuery(id+"F8.imprint","INTERSECT",VERTEX,{"derivedFrom":[subQ1,subQ0]});Q15=makeQuery(id+"F8.imprint","IMPRINT",FACE,{"disambiguationData":[TD([[makeQuery(id+"F8.imprint","IMPRINT",EDGE,{"disambiguationData":[TD([[subQ2,-1.0]])],"derivedFrom":subQ1}),1.0]])]});}
            var Q16;
            {var subQ0=sQuery(id+"F8.wireOp",EDGE,"E140.filletArc");Q16=makeQuery(id+"F8.imprint","IMPRINT",FACE,{"disambiguationData":[TD([[makeQuery(id+"F8.imprint","IMPRINT",EDGE,{"derivedFrom":subQ0}),1.0]])]});}
            var Q17;
            {var subQ0=sQuery(id+"F8.wireOp",EDGE,"E139.filletArc");Q17=makeQuery(id+"F8.imprint","IMPRINT",FACE,{"disambiguationData":[TD([[makeQuery(id+"F8.imprint","IMPRINT",EDGE,{"derivedFrom":subQ0}),1.0]])]});}
            var Q18;
            {var subQ0=sQuery(id+"F8.wireOp",EDGE,"E142.filletArc");Q18=makeQuery(id+"F8.imprint","IMPRINT",FACE,{"disambiguationData":[TD([[makeQuery(id+"F8.imprint","IMPRINT",EDGE,{"derivedFrom":subQ0}),1.0]])]});}
            var Q19;
            {var subQ0=sQuery(id+"F8.wireOp",EDGE,"E141.filletArc");Q19=makeQuery(id+"F8.imprint","IMPRINT",FACE,{"disambiguationData":[TD([[makeQuery(id+"F8.imprint","IMPRINT",EDGE,{"derivedFrom":subQ0}),1.0]])]});}
            var Q20;
            {var subQ0=sQuery(id+"F8.wireOp",EDGE,"E130.left");var subQ1=sQuery(id+"F8.wireOp",EDGE,"E111");var subQ2=makeQuery(id+"F8.imprint","INTERSECT",VERTEX,{"derivedFrom":[subQ1,subQ0]});Q20=makeQuery(id+"F8.imprint","IMPRINT",FACE,{"disambiguationData":[TD([[makeQuery(id+"F8.imprint","IMPRINT",EDGE,{"disambiguationData":[TD([[subQ2,-1.0]])],"derivedFrom":subQ1}),1.0]])]});}
            var Q21;
            {var subQ0=sQuery(id+"F8.wireOp",EDGE,"E120");var subQ1=sQuery(id+"F8.wireOp",EDGE,"E111");var subQ2=makeQuery(id+"F8.imprint","INTERSECT",VERTEX,{"derivedFrom":[subQ1,subQ0]});Q21=makeQuery(id+"F8.imprint","IMPRINT",FACE,{"disambiguationData":[TD([[makeQuery(id+"F8.imprint","IMPRINT",EDGE,{"disambiguationData":[TD([[subQ2,-1.0]])],"derivedFrom":subQ1}),1.0]])]});}
            var Q22;
            {var subQ0=sQuery(id+"F8.wireOp",EDGE,"E130.left");var subQ1=sQuery(id+"F8.wireOp",EDGE,"E110");var subQ2=makeQuery(id+"F8.imprint","INTERSECT",VERTEX,{"derivedFrom":[subQ1,subQ0]});Q22=makeQuery(id+"F8.imprint","IMPRINT",FACE,{"disambiguationData":[TD([[makeQuery(id+"F8.imprint","IMPRINT",EDGE,{"disambiguationData":[TD([[subQ2,-1.0]])],"derivedFrom":subQ1}),1.0]])]});}
            var Q23;
            {var subQ0=sQuery(id+"F8.wireOp",EDGE,"E120");var subQ1=sQuery(id+"F8.wireOp",EDGE,"E110");var subQ2=makeQuery(id+"F8.imprint","INTERSECT",VERTEX,{"derivedFrom":[subQ1,subQ0]});Q23=makeQuery(id+"F8.imprint","IMPRINT",FACE,{"disambiguationData":[TD([[makeQuery(id+"F8.imprint","IMPRINT",EDGE,{"disambiguationData":[TD([[subQ2,-1.0]])],"derivedFrom":subQ1}),1.0]])]});}
            var Q24;
            {var subQ0=sQuery(id+"F8.wireOp",EDGE,"E144.filletArc");Q24=makeQuery(id+"F8.imprint","IMPRINT",FACE,{"disambiguationData":[TD([[makeQuery(id+"F8.imprint","IMPRINT",EDGE,{"derivedFrom":subQ0}),1.0]])]});}
            var Q25;
            {var subQ0=sQuery(id+"F8.wireOp",EDGE,"E143.filletArc");Q25=makeQuery(id+"F8.imprint","IMPRINT",FACE,{"disambiguationData":[TD([[makeQuery(id+"F8.imprint","IMPRINT",EDGE,{"derivedFrom":subQ0}),1.0]])]});}
            extrude(context, id + "F10", {"entities" : qUnion([Q0, Q1, Q2, Q3, Q4, Q5, Q6, Q7, Q8, Q9, Q10, Q11, Q12, Q13, Q14, Q15, Q16, Q17, Q18, Q19, Q20, Q21, Q22, Q23, Q24, Q25]), "operationType" : NewBodyOperationType.REMOVE, "oppositeDirection" : true, "depth" : 75 * mm});
        }
        {
            var Q0;
            {var subQ0=sQuery(id+"F5.wireOp",EDGE,"E98.filletArc");Q0=makeQuery(id+"F5.imprint","IMPRINT",FACE,{"disambiguationData":[TD([[makeQuery(id+"F5.imprint","IMPRINT",EDGE,{"derivedFrom":subQ0}),1.0]])]});}
            var Q1;
            {var subQ0=sQuery(id+"F5.wireOp",EDGE,"E99.filletArc");Q1=makeQuery(id+"F5.imprint","IMPRINT",FACE,{"disambiguationData":[TD([[makeQuery(id+"F5.imprint","IMPRINT",EDGE,{"derivedFrom":subQ0}),1.0]])]});}
            var Q2;
            {var subQ0=sQuery(id+"F5.wireOp",EDGE,"E76");var subQ1=sQuery(id+"F5.wireOp",EDGE,"E75");var subQ2=makeQuery(id+"F5.imprint","INTERSECT",VERTEX,{"derivedFrom":[subQ1,subQ0]});Q2=makeQuery(id+"F5.imprint","IMPRINT",FACE,{"disambiguationData":[TD([[makeQuery(id+"F5.imprint","IMPRINT",EDGE,{"disambiguationData":[TD([[subQ2,-1.0]])],"derivedFrom":subQ1}),1.0]])]});}
            var Q3;
            {var subQ0=sQuery(id+"F5.wireOp",EDGE,"E76");var subQ1=sQuery(id+"F5.wireOp",EDGE,"E75");var subQ2=makeQuery(id+"F5.imprint","INTERSECT",VERTEX,{"derivedFrom":[subQ1,subQ0]});Q3=makeQuery(id+"F5.imprint","IMPRINT",FACE,{"disambiguationData":[TD([[makeQuery(id+"F5.imprint","IMPRINT",EDGE,{"disambiguationData":[TD([[subQ2,-1.0]])],"derivedFrom":subQ1}),-1.0]])]});}
            var Q4;
            {var subQ0=sQuery(id+"F5.wireOp",EDGE,"E84");var subQ1=sQuery(id+"F5.wireOp",EDGE,"E75");var subQ2=makeQuery(id+"F5.imprint","INTERSECT",VERTEX,{"derivedFrom":[subQ1,subQ0]});Q4=makeQuery(id+"F5.imprint","IMPRINT",FACE,{"disambiguationData":[TD([[makeQuery(id+"F5.imprint","IMPRINT",EDGE,{"disambiguationData":[TD([[subQ2,-1.0]])],"derivedFrom":subQ1}),1.0]])]});}
            var Q5;
            {var subQ0=sQuery(id+"F5.wireOp",EDGE,"E84");var subQ1=sQuery(id+"F5.wireOp",EDGE,"E75");var subQ2=makeQuery(id+"F5.imprint","INTERSECT",VERTEX,{"derivedFrom":[subQ1,subQ0]});Q5=makeQuery(id+"F5.imprint","IMPRINT",FACE,{"disambiguationData":[TD([[makeQuery(id+"F5.imprint","IMPRINT",EDGE,{"disambiguationData":[TD([[subQ2,-1.0]])],"derivedFrom":subQ1}),-1.0]])]});}
            var Q6;
            {var subQ0=sQuery(id+"F5.wireOp",EDGE,"E77");var subQ1=sQuery(id+"F5.wireOp",EDGE,"E75");var subQ2=makeQuery(id+"F5.imprint","INTERSECT",VERTEX,{"derivedFrom":[subQ1,subQ0]});Q6=makeQuery(id+"F5.imprint","IMPRINT",FACE,{"disambiguationData":[TD([[makeQuery(id+"F5.imprint","IMPRINT",EDGE,{"disambiguationData":[TD([[subQ2,-1.0]])],"derivedFrom":subQ1}),1.0]])]});}
            var Q7;
            {var subQ0=sQuery(id+"F5.wireOp",EDGE,"E77");var subQ1=sQuery(id+"F5.wireOp",EDGE,"E75");var subQ2=makeQuery(id+"F5.imprint","INTERSECT",VERTEX,{"derivedFrom":[subQ1,subQ0]});Q7=makeQuery(id+"F5.imprint","IMPRINT",FACE,{"disambiguationData":[TD([[makeQuery(id+"F5.imprint","IMPRINT",EDGE,{"disambiguationData":[TD([[subQ2,-1.0]])],"derivedFrom":subQ1}),-1.0]])]});}
            var Q8;
            {var subQ0=sQuery(id+"F5.wireOp",EDGE,"E101.filletArc");Q8=makeQuery(id+"F5.imprint","IMPRINT",FACE,{"disambiguationData":[TD([[makeQuery(id+"F5.imprint","IMPRINT",EDGE,{"derivedFrom":subQ0}),1.0]])]});}
            var Q9;
            {var subQ0=sQuery(id+"F5.wireOp",EDGE,"E100.filletArc");Q9=makeQuery(id+"F5.imprint","IMPRINT",FACE,{"disambiguationData":[TD([[makeQuery(id+"F5.imprint","IMPRINT",EDGE,{"derivedFrom":subQ0}),1.0]])]});}
            var Q10;
            {var subQ0=sQuery(id+"F5.wireOp",EDGE,"E102.filletArc");Q10=makeQuery(id+"F5.imprint","IMPRINT",FACE,{"disambiguationData":[TD([[makeQuery(id+"F5.imprint","IMPRINT",EDGE,{"derivedFrom":subQ0}),1.0]])]});}
            var Q11;
            {var subQ0=sQuery(id+"F5.wireOp",EDGE,"E103.filletArc");Q11=makeQuery(id+"F5.imprint","IMPRINT",FACE,{"disambiguationData":[TD([[makeQuery(id+"F5.imprint","IMPRINT",EDGE,{"derivedFrom":subQ0}),1.0]])]});}
            var Q12;
            {var subQ0=sQuery(id+"F5.wireOp",EDGE,"E79");var subQ1=sQuery(id+"F5.wireOp",EDGE,"E75");var subQ2=makeQuery(id+"F5.imprint","INTERSECT",VERTEX,{"derivedFrom":[subQ1,subQ0]});Q12=makeQuery(id+"F5.imprint","IMPRINT",FACE,{"disambiguationData":[TD([[makeQuery(id+"F5.imprint","IMPRINT",EDGE,{"disambiguationData":[TD([[subQ2,-1.0]])],"derivedFrom":subQ1}),-1.0]])]});}
            var Q13;
            {var subQ0=sQuery(id+"F5.wireOp",EDGE,"E79");var subQ1=sQuery(id+"F5.wireOp",EDGE,"E75");var subQ2=makeQuery(id+"F5.imprint","INTERSECT",VERTEX,{"derivedFrom":[subQ1,subQ0]});Q13=makeQuery(id+"F5.imprint","IMPRINT",FACE,{"disambiguationData":[TD([[makeQuery(id+"F5.imprint","IMPRINT",EDGE,{"disambiguationData":[TD([[subQ2,-1.0]])],"derivedFrom":subQ1}),1.0]])]});}
            var Q14;
            {var subQ0=sQuery(id+"F5.wireOp",EDGE,"E81");var subQ1=sQuery(id+"F5.wireOp",EDGE,"E75");var subQ2=makeQuery(id+"F5.imprint","INTERSECT",VERTEX,{"derivedFrom":[subQ1,subQ0]});Q14=makeQuery(id+"F5.imprint","IMPRINT",FACE,{"disambiguationData":[TD([[makeQuery(id+"F5.imprint","IMPRINT",EDGE,{"disambiguationData":[TD([[subQ2,-1.0]])],"derivedFrom":subQ1}),1.0]])]});}
            var Q15;
            {var subQ0=sQuery(id+"F5.wireOp",EDGE,"E81");var subQ1=sQuery(id+"F5.wireOp",EDGE,"E75");var subQ2=makeQuery(id+"F5.imprint","INTERSECT",VERTEX,{"derivedFrom":[subQ1,subQ0]});Q15=makeQuery(id+"F5.imprint","IMPRINT",FACE,{"disambiguationData":[TD([[makeQuery(id+"F5.imprint","IMPRINT",EDGE,{"disambiguationData":[TD([[subQ2,-1.0]])],"derivedFrom":subQ1}),-1.0]])]});}
            var Q16;
            {var subQ0=sQuery(id+"F5.wireOp",EDGE,"E104.filletArc");Q16=makeQuery(id+"F5.imprint","IMPRINT",FACE,{"disambiguationData":[TD([[makeQuery(id+"F5.imprint","IMPRINT",EDGE,{"derivedFrom":subQ0}),1.0]])]});}
            var Q17;
            {var subQ0=sQuery(id+"F5.wireOp",EDGE,"E105.filletArc");Q17=makeQuery(id+"F5.imprint","IMPRINT",FACE,{"disambiguationData":[TD([[makeQuery(id+"F5.imprint","IMPRINT",EDGE,{"derivedFrom":subQ0}),1.0]])]});}
            var Q18;
            {var subQ0=sQuery(id+"F5.wireOp",EDGE,"E107.filletArc");Q18=makeQuery(id+"F5.imprint","IMPRINT",FACE,{"disambiguationData":[TD([[makeQuery(id+"F5.imprint","IMPRINT",EDGE,{"derivedFrom":subQ0}),1.0]])]});}
            var Q19;
            {var subQ0=sQuery(id+"F5.wireOp",EDGE,"E106.filletArc");Q19=makeQuery(id+"F5.imprint","IMPRINT",FACE,{"disambiguationData":[TD([[makeQuery(id+"F5.imprint","IMPRINT",EDGE,{"derivedFrom":subQ0}),1.0]])]});}
            var Q20;
            {var subQ0=sQuery(id+"F5.wireOp",EDGE,"E82");var subQ1=sQuery(id+"F5.wireOp",EDGE,"E75");var subQ2=makeQuery(id+"F5.imprint","INTERSECT",VERTEX,{"derivedFrom":[subQ1,subQ0]});Q20=makeQuery(id+"F5.imprint","IMPRINT",FACE,{"disambiguationData":[TD([[makeQuery(id+"F5.imprint","IMPRINT",EDGE,{"disambiguationData":[TD([[subQ2,-1.0]])],"derivedFrom":subQ1}),-1.0]])]});}
            var Q21;
            {var subQ0=sQuery(id+"F5.wireOp",EDGE,"E82");var subQ1=sQuery(id+"F5.wireOp",EDGE,"E75");var subQ2=makeQuery(id+"F5.imprint","INTERSECT",VERTEX,{"derivedFrom":[subQ1,subQ0]});Q21=makeQuery(id+"F5.imprint","IMPRINT",FACE,{"disambiguationData":[TD([[makeQuery(id+"F5.imprint","IMPRINT",EDGE,{"disambiguationData":[TD([[subQ2,-1.0]])],"derivedFrom":subQ1}),1.0]])]});}
            var Q22;
            {var subQ0=sQuery(id+"F5.wireOp",EDGE,"E83");var subQ1=sQuery(id+"F5.wireOp",EDGE,"E75");var subQ2=makeQuery(id+"F5.imprint","INTERSECT",VERTEX,{"derivedFrom":[subQ1,subQ0]});Q22=makeQuery(id+"F5.imprint","IMPRINT",FACE,{"disambiguationData":[TD([[makeQuery(id+"F5.imprint","IMPRINT",EDGE,{"disambiguationData":[TD([[subQ2,-1.0]])],"derivedFrom":subQ1}),1.0]])]});}
            var Q23;
            {var subQ0=sQuery(id+"F5.wireOp",EDGE,"E83");var subQ1=sQuery(id+"F5.wireOp",EDGE,"E75");var subQ2=makeQuery(id+"F5.imprint","INTERSECT",VERTEX,{"derivedFrom":[subQ1,subQ0]});Q23=makeQuery(id+"F5.imprint","IMPRINT",FACE,{"disambiguationData":[TD([[makeQuery(id+"F5.imprint","IMPRINT",EDGE,{"disambiguationData":[TD([[subQ2,-1.0]])],"derivedFrom":subQ1}),-1.0]])]});}
            var Q24;
            {var subQ0=sQuery(id+"F5.wireOp",EDGE,"E109.filletArc");Q24=makeQuery(id+"F5.imprint","IMPRINT",FACE,{"disambiguationData":[TD([[makeQuery(id+"F5.imprint","IMPRINT",EDGE,{"derivedFrom":subQ0}),1.0]])]});}
            var Q25;
            {var subQ0=sQuery(id+"F5.wireOp",EDGE,"E108.filletArc");Q25=makeQuery(id+"F5.imprint","IMPRINT",FACE,{"disambiguationData":[TD([[makeQuery(id+"F5.imprint","IMPRINT",EDGE,{"derivedFrom":subQ0}),1.0]])]});}
            extrude(context, id + "F11", {"entities" : qUnion([Q0, Q1, Q2, Q3, Q4, Q5, Q6, Q7, Q8, Q9, Q10, Q11, Q12, Q13, Q14, Q15, Q16, Q17, Q18, Q19, Q20, Q21, Q22, Q23, Q24, Q25]), "operationType" : NewBodyOperationType.REMOVE, "oppositeDirection" : true, "depth" : 75 * mm});
        }
        {
            var Q0;
            Q0=makeQuery(id+"F1.opExtrude","CAP_FACE",FACE,{"disambiguationData":[OSD([sQuery(id+"F0.wireOp",EDGE,"E0.bottom"),sQuery(id+"F0.wireOp",EDGE,"E0.top"),sQuery(id+"F0.wireOp",EDGE,"E0.left"),sQuery(id+"F0.wireOp",EDGE,"E0.right"),sQuery(id+"F0.wireOp",EDGE,"E1.bottom"),sQuery(id+"F0.wireOp",EDGE,"E1.top"),sQuery(id+"F0.wireOp",EDGE,"E1.left"),sQuery(id+"F0.wireOp",EDGE,"E1.right"),sQuery(id+"F0.wireOp",EDGE,"E2.filletArc"),sQuery(id+"F0.wireOp",EDGE,"E3.filletArc"),sQuery(id+"F0.wireOp",EDGE,"E4.filletArc"),sQuery(id+"F0.wireOp",EDGE,"E5.filletArc")])],"isStart":false});
            var sketch = newSketch(context, id + "F12", { "sketchPlane" : qUnion([Q0])});
            skLineSegment(sketch, "E145", {"start": v(-45, 789.91) * mm, "end": v(-45, -210.09) * mm});
            skLineSegment(sketch, "E146", {"start": v(630, 789.91) * mm, "end": v(630, -210.09) * mm});
            skLineSegment(sketch, "E147", {"start": v(-167.5, -115.09) * mm, "end": v(752.5, -115.09) * mm});
            skLineSegment(sketch, "E148", {"start": v(-167.5, -95.09) * mm, "end": v(752.5, -95.09) * mm});
            skLineSegment(sketch, "E149", {"start": v(-167.5, -0.09) * mm, "end": v(752.5, -0.09) * mm});
            skLineSegment(sketch, "E150", {"start": v(-167.5, 94.91) * mm, "end": v(752.5, 94.91) * mm});
            skLineSegment(sketch, "E151", {"start": v(-167.5, 189.91) * mm, "end": v(752.5, 189.91) * mm});
            skLineSegment(sketch, "E152", {"start": v(-167.5, 284.91) * mm, "end": v(752.5, 284.91) * mm});
            skLineSegment(sketch, "E153", {"start": v(-167.5, 379.91) * mm, "end": v(752.5, 379.91) * mm});
            skLineSegment(sketch, "E154", {"start": v(-167.5, 474.91) * mm, "end": v(752.5, 474.91) * mm});
            skLineSegment(sketch, "E155", {"start": v(-167.5, 569.91) * mm, "end": v(752.5, 569.91) * mm});
            skLineSegment(sketch, "E156", {"start": v(-167.5, 664.91) * mm, "end": v(752.5, 664.91) * mm});
            skPoint(sketch, "E157", {"position": v(-45, 664.91) * mm});
            skPoint(sketch, "E158", {"position": v(-45, 569.91) * mm});
            skPoint(sketch, "E159", {"position": v(-45, 474.91) * mm});
            skPoint(sketch, "E160", {"position": v(-45, 379.91) * mm});
            skPoint(sketch, "E161", {"position": v(-45, 284.91) * mm});
            skPoint(sketch, "E162", {"position": v(-45, 189.91) * mm});
            skPoint(sketch, "E163", {"position": v(-45, 94.91) * mm});
            skPoint(sketch, "E164", {"position": v(-45, -0.09) * mm});
            skPoint(sketch, "E165", {"position": v(-45, -95.09) * mm});
            skPoint(sketch, "E166", {"position": v(630, 664.91) * mm});
            skPoint(sketch, "E167", {"position": v(630, 569.91) * mm});
            skPoint(sketch, "E168", {"position": v(630, 474.91) * mm});
            skPoint(sketch, "E169", {"position": v(630, 379.91) * mm});
            skPoint(sketch, "E170", {"position": v(630, 284.91) * mm});
            skPoint(sketch, "E171", {"position": v(630, 189.91) * mm});
            skPoint(sketch, "E172", {"position": v(630, 94.91) * mm});
            skPoint(sketch, "E173", {"position": v(630, -0.09) * mm});
            skPoint(sketch, "E174", {"position": v(630, -95.09) * mm});
            skSolve(sketch);
        }
        {
            var Q0;
            Q0=sQuery(id+"F12.wireOp",VERTEX,"E157");
            var Q1;
            Q1=sQuery(id+"F12.wireOp",VERTEX,"E158");
            var Q2;
            Q2=sQuery(id+"F12.wireOp",VERTEX,"E159");
            var Q3;
            Q3=sQuery(id+"F12.wireOp",VERTEX,"E160");
            var Q4;
            Q4=sQuery(id+"F12.wireOp",VERTEX,"E161");
            var Q5;
            Q5=sQuery(id+"F12.wireOp",VERTEX,"E162");
            var Q6;
            Q6=sQuery(id+"F12.wireOp",VERTEX,"E163");
            var Q7;
            Q7=sQuery(id+"F12.wireOp",VERTEX,"E164");
            var Q8;
            Q8=sQuery(id+"F12.wireOp",VERTEX,"E165");
            var Q9;
            Q9=sQuery(id+"F12.wireOp",VERTEX,"E174");
            var Q10;
            Q10=sQuery(id+"F12.wireOp",VERTEX,"E173");
            var Q11;
            Q11=sQuery(id+"F12.wireOp",VERTEX,"E172");
            var Q12;
            Q12=sQuery(id+"F12.wireOp",VERTEX,"E171");
            var Q13;
            Q13=sQuery(id+"F12.wireOp",VERTEX,"E170");
            var Q14;
            Q14=sQuery(id+"F12.wireOp",VERTEX,"E169");
            var Q15;
            Q15=sQuery(id+"F12.wireOp",VERTEX,"E168");
            var Q16;
            Q16=sQuery(id+"F12.wireOp",VERTEX,"E167");
            var Q17;
            Q17=sQuery(id+"F12.wireOp",VERTEX,"E166");
            var Q18;
            Q18=makeQuery(id+"F1.opExtrude","SWEPT_BODY",BODY,{"disambiguationData":[OSD([sQuery(id+"F0.wireOp",EDGE,"E0.bottom"),sQuery(id+"F0.wireOp",EDGE,"E0.top"),sQuery(id+"F0.wireOp",EDGE,"E0.left"),sQuery(id+"F0.wireOp",EDGE,"E0.right"),sQuery(id+"F0.wireOp",EDGE,"E1.bottom"),sQuery(id+"F0.wireOp",EDGE,"E1.top"),sQuery(id+"F0.wireOp",EDGE,"E1.left"),sQuery(id+"F0.wireOp",EDGE,"E1.right"),sQuery(id+"F0.wireOp",EDGE,"E2.filletArc"),sQuery(id+"F0.wireOp",EDGE,"E3.filletArc"),sQuery(id+"F0.wireOp",EDGE,"E4.filletArc"),sQuery(id+"F0.wireOp",EDGE,"E5.filletArc")])]});
            hole(context, id + "F13", {"style" : HoleStyle.SIMPLE, "endStyle" : HoleEndStyle.THROUGH, "holeDiameter" : 9 * mm, "locations" : qUnion([Q0, Q1, Q2, Q3, Q4, Q5, Q6, Q7, Q8, Q9, Q10, Q11, Q12, Q13, Q14, Q15, Q16, Q17]), "scope" : qUnion([Q18]), "isTappedThrough" : true});
        }
        {
            var Q0;
            Q0=qCreatedBy(makeId("Right.planeOp"),FACE);
            var sketch = newSketch(context, id + "F14", { "sketchPlane" : qUnion([Q0])});
            skLineSegment(sketch, "E175.bottom", {"start": v(-354, 68.59) * mm, "end": v(-414.8, 68.59) * mm});
            skLineSegment(sketch, "E175.top", {"start": v(-354, -11.41) * mm, "end": v(-414.8, -11.41) * mm});
            skLineSegment(sketch, "E175.left", {"start": v(-344.4, 58.99) * mm, "end": v(-344.4, -1.81) * mm});
            skLineSegment(sketch, "E175.right", {"start": v(-424.4, 58.99) * mm, "end": v(-424.4, -1.81) * mm});
            skLineSegment(sketch, "E176.bottom", {"start": v(-356.3, 66.29) * mm, "end": v(-412.5, 66.29) * mm});
            skLineSegment(sketch, "E176.top", {"start": v(-356.3, -9.11) * mm, "end": v(-412.5, -9.11) * mm});
            skLineSegment(sketch, "E176.left", {"start": v(-346.7, 56.69) * mm, "end": v(-346.7, 0.49) * mm});
            skLineSegment(sketch, "E176.right", {"start": v(-422.1, 56.69) * mm, "end": v(-422.1, 0.49) * mm});
            skPoint(sketch, "E177.visualSharp", {"position": v(-346.7, 66.29) * mm});
            skArc(sketch, "E177.filletArc", {"start": v(-346.7, 56.69) * mm, "mid": v(-349.52, 63.48) * mm, "end": v(-356.3, 66.29) * mm});
            skPoint(sketch, "E178.visualSharp", {"position": v(-422.1, 66.29) * mm});
            skArc(sketch, "E178.filletArc", {"start": v(-412.5, 66.29) * mm, "mid": v(-419.3, 63.48) * mm, "end": v(-422.1, 56.69) * mm});
            skPoint(sketch, "E179.visualSharp", {"position": v(-422.1, -9.11) * mm});
            skArc(sketch, "E179.filletArc", {"start": v(-422.1, 0.49) * mm, "mid": v(-419.3, -6.3) * mm, "end": v(-412.5, -9.11) * mm});
            skPoint(sketch, "E180.visualSharp", {"position": v(-346.7, -9.11) * mm});
            skArc(sketch, "E180.filletArc", {"start": v(-356.3, -9.11) * mm, "mid": v(-349.52, -6.3) * mm, "end": v(-346.7, 0.49) * mm});
            skPoint(sketch, "E181.visualSharp", {"position": v(-344.4, 68.59) * mm});
            skArc(sketch, "E181.filletArc", {"start": v(-344.4, 58.99) * mm, "mid": v(-347.22, 65.78) * mm, "end": v(-354, 68.59) * mm});
            skPoint(sketch, "E182.visualSharp", {"position": v(-424.4, 68.59) * mm});
            skArc(sketch, "E182.filletArc", {"start": v(-414.8, 68.59) * mm, "mid": v(-421.6, 65.78) * mm, "end": v(-424.4, 58.99) * mm});
            skPoint(sketch, "E183.visualSharp", {"position": v(-424.4, -11.41) * mm});
            skArc(sketch, "E183.filletArc", {"start": v(-424.4, -1.81) * mm, "mid": v(-421.6, -8.6) * mm, "end": v(-414.8, -11.41) * mm});
            skPoint(sketch, "E184.visualSharp", {"position": v(-344.4, -11.41) * mm});
            skArc(sketch, "E184.filletArc", {"start": v(-354, -11.41) * mm, "mid": v(-347.22, -8.6) * mm, "end": v(-344.4, -1.81) * mm});
            skSolve(sketch);
        }
        {
            var Q0;
            Q0=makeQuery(id+"F14.imprint","IMPRINT",FACE,{"disambiguationData":[TD([[makeQuery(id+"F14.imprint","IMPRINT",EDGE,{"derivedFrom":sQuery(id+"F14.wireOp",EDGE,"E175.bottom")}),1.0]])]});
            extrude(context, id + "F15", {"entities" : qUnion([Q0]), "depth" : 1000 * mm});
        }
        {
            var Q0;
            Q0=makeQuery(id+"F15.opExtrude","SWEPT_BODY",BODY,{"disambiguationData":[OSD([sQuery(id+"F14.wireOp",EDGE,"E175.bottom"),sQuery(id+"F14.wireOp",EDGE,"E175.top"),sQuery(id+"F14.wireOp",EDGE,"E175.left"),sQuery(id+"F14.wireOp",EDGE,"E175.right"),sQuery(id+"F14.wireOp",EDGE,"E176.bottom"),sQuery(id+"F14.wireOp",EDGE,"E176.top"),sQuery(id+"F14.wireOp",EDGE,"E176.left"),sQuery(id+"F14.wireOp",EDGE,"E176.right"),sQuery(id+"F14.wireOp",EDGE,"E177.filletArc"),sQuery(id+"F14.wireOp",EDGE,"E178.filletArc"),sQuery(id+"F14.wireOp",EDGE,"E179.filletArc"),sQuery(id+"F14.wireOp",EDGE,"E180.filletArc"),sQuery(id+"F14.wireOp",EDGE,"E181.filletArc"),sQuery(id+"F14.wireOp",EDGE,"E182.filletArc"),sQuery(id+"F14.wireOp",EDGE,"E183.filletArc"),sQuery(id+"F14.wireOp",EDGE,"E184.filletArc")])]});
            transform(context, id + "F16", {"entities" : qUnion([Q0]), "transformType" : TransformType.TRANSLATION_3D, "dx" : 0 * mm, "dy" : -246 * mm, "dz" : 0 * mm, "makeCopy" : true});
        }
        {
            var Q0;
            Q0=makeQuery(id+"F16.opPattern","COPY",FACE,{"derivedFrom":makeQuery(id+"F15.opExtrude","CAP_FACE",FACE,{"disambiguationData":[OSD([sQuery(id+"F14.wireOp",EDGE,"E175.bottom"),sQuery(id+"F14.wireOp",EDGE,"E175.top"),sQuery(id+"F14.wireOp",EDGE,"E175.left"),sQuery(id+"F14.wireOp",EDGE,"E175.right"),sQuery(id+"F14.wireOp",EDGE,"E176.bottom"),sQuery(id+"F14.wireOp",EDGE,"E176.top"),sQuery(id+"F14.wireOp",EDGE,"E176.left"),sQuery(id+"F14.wireOp",EDGE,"E176.right"),sQuery(id+"F14.wireOp",EDGE,"E177.filletArc"),sQuery(id+"F14.wireOp",EDGE,"E178.filletArc"),sQuery(id+"F14.wireOp",EDGE,"E179.filletArc"),sQuery(id+"F14.wireOp",EDGE,"E180.filletArc"),sQuery(id+"F14.wireOp",EDGE,"E181.filletArc"),sQuery(id+"F14.wireOp",EDGE,"E182.filletArc"),sQuery(id+"F14.wireOp",EDGE,"E183.filletArc"),sQuery(id+"F14.wireOp",EDGE,"E184.filletArc")])],"isStart":false}),"instanceName":"1"});
            extrude(context, id + "F17", {"entities" : qUnion([Q0]), "operationType" : NewBodyOperationType.REMOVE, "oppositeDirection" : true, "depth" : 300 * mm});
        }
        {
            var Q0;
            Q0=makeQuery(id+"F16.opPattern","COPY",BODY,{"derivedFrom":makeQuery(id+"F15.opExtrude","SWEPT_BODY",BODY,{"disambiguationData":[OSD([sQuery(id+"F14.wireOp",EDGE,"E175.bottom"),sQuery(id+"F14.wireOp",EDGE,"E175.top"),sQuery(id+"F14.wireOp",EDGE,"E175.left"),sQuery(id+"F14.wireOp",EDGE,"E175.right"),sQuery(id+"F14.wireOp",EDGE,"E176.bottom"),sQuery(id+"F14.wireOp",EDGE,"E176.top"),sQuery(id+"F14.wireOp",EDGE,"E176.left"),sQuery(id+"F14.wireOp",EDGE,"E176.right"),sQuery(id+"F14.wireOp",EDGE,"E177.filletArc"),sQuery(id+"F14.wireOp",EDGE,"E178.filletArc"),sQuery(id+"F14.wireOp",EDGE,"E179.filletArc"),sQuery(id+"F14.wireOp",EDGE,"E180.filletArc"),sQuery(id+"F14.wireOp",EDGE,"E181.filletArc"),sQuery(id+"F14.wireOp",EDGE,"E182.filletArc"),sQuery(id+"F14.wireOp",EDGE,"E183.filletArc"),sQuery(id+"F14.wireOp",EDGE,"E184.filletArc")])]}),"instanceName":"1"});
            transform(context, id + "F18", {"entities" : qUnion([Q0]), "transformType" : TransformType.TRANSLATION_3D, "dx" : 0 * mm, "dy" : -288 * mm, "dz" : 0 * mm, "makeCopy" : true});
        }
        {
            var Q0;
            Q0=makeQuery(id+"F18.opPattern","COPY",FACE,{"derivedFrom":makeQuery(id+"F17.boolean.opBoolean","COPY",FACE,{"derivedFrom":makeQuery(id+"F17.opExtrude","CAP_FACE",FACE,{"disambiguationData":[OSD([sQuery(id+"F14.wireOp",EDGE,"E175.bottom"),sQuery(id+"F14.wireOp",EDGE,"E175.top"),sQuery(id+"F14.wireOp",EDGE,"E175.left"),sQuery(id+"F14.wireOp",EDGE,"E175.right"),sQuery(id+"F14.wireOp",EDGE,"E176.bottom"),sQuery(id+"F14.wireOp",EDGE,"E176.top"),sQuery(id+"F14.wireOp",EDGE,"E176.left"),sQuery(id+"F14.wireOp",EDGE,"E176.right"),sQuery(id+"F14.wireOp",EDGE,"E177.filletArc"),sQuery(id+"F14.wireOp",EDGE,"E178.filletArc"),sQuery(id+"F14.wireOp",EDGE,"E179.filletArc"),sQuery(id+"F14.wireOp",EDGE,"E180.filletArc"),sQuery(id+"F14.wireOp",EDGE,"E181.filletArc"),sQuery(id+"F14.wireOp",EDGE,"E182.filletArc"),sQuery(id+"F14.wireOp",EDGE,"E183.filletArc"),sQuery(id+"F14.wireOp",EDGE,"E184.filletArc")])],"isStart":false})}),"instanceName":"1"});
            extrude(context, id + "F19", {"entities" : qUnion([Q0]), "operationType" : NewBodyOperationType.REMOVE, "oppositeDirection" : true, "depth" : 490 * mm});
        }
        {
            var Q0;
            Q0=makeQuery(id+"F15.opExtrude","CAP_FACE",FACE,{"disambiguationData":[OSD([sQuery(id+"F14.wireOp",EDGE,"E175.bottom"),sQuery(id+"F14.wireOp",EDGE,"E175.top"),sQuery(id+"F14.wireOp",EDGE,"E175.left"),sQuery(id+"F14.wireOp",EDGE,"E175.right"),sQuery(id+"F14.wireOp",EDGE,"E176.bottom"),sQuery(id+"F14.wireOp",EDGE,"E176.top"),sQuery(id+"F14.wireOp",EDGE,"E176.left"),sQuery(id+"F14.wireOp",EDGE,"E176.right"),sQuery(id+"F14.wireOp",EDGE,"E177.filletArc"),sQuery(id+"F14.wireOp",EDGE,"E178.filletArc"),sQuery(id+"F14.wireOp",EDGE,"E179.filletArc"),sQuery(id+"F14.wireOp",EDGE,"E180.filletArc"),sQuery(id+"F14.wireOp",EDGE,"E181.filletArc"),sQuery(id+"F14.wireOp",EDGE,"E182.filletArc"),sQuery(id+"F14.wireOp",EDGE,"E183.filletArc"),sQuery(id+"F14.wireOp",EDGE,"E184.filletArc")])],"isStart":false});
            extrude(context, id + "F20", {"entities" : qUnion([Q0]), "operationType" : NewBodyOperationType.REMOVE, "oppositeDirection" : true, "depth" : 120 * mm});
        }
        {
            var Q0;
            Q0 = qSketchRegion(id + "F0", true);
            extrude(context, id + "F21", {"entities" : qUnion([Q0]), "depth" : 5 * mm});
        }
    });
